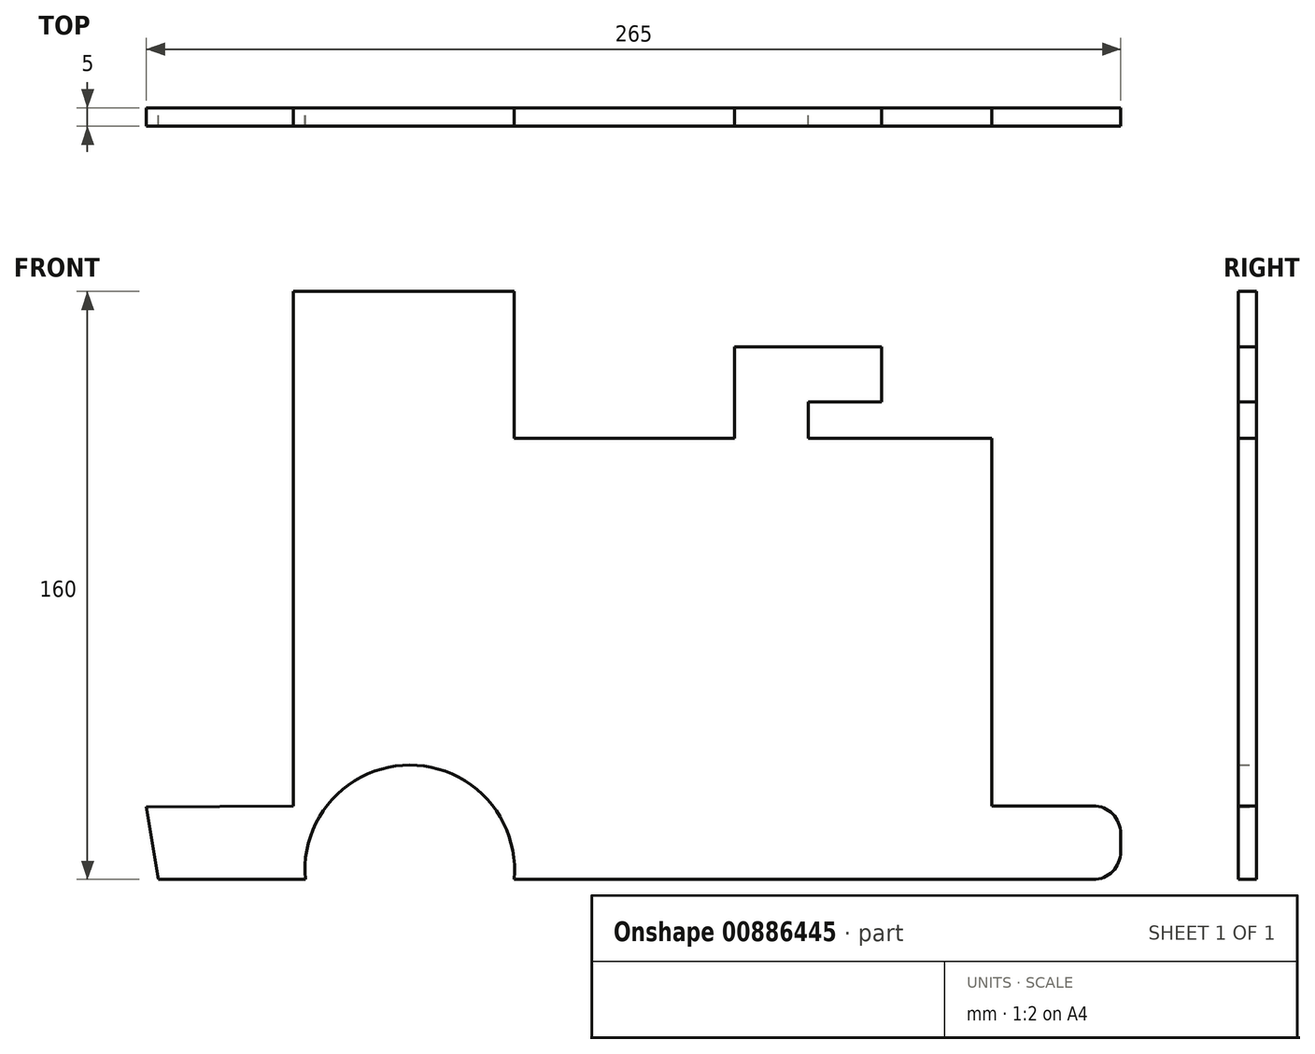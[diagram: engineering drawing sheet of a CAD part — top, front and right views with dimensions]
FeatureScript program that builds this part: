
annotation { "Feature Type Name" : "Feature", "Feature Type Description" : "" }
export const myFeature = defineFeature(function(context is Context, id is Id, definition is map)
    precondition{}
    {
        {
            var Q0;
            Q0=qCreatedBy(makeId("Front.planeOp"),FACE);
            var sketch = newSketch(context, id + "F0", { "sketchPlane" : qUnion([Q0])});
            skLineSegment(sketch, "E0.bottom", {"start": v(-65, 89.5) * mm, "end": v(-5, 89.5) * mm});
            skLineSegment(sketch, "E0.left", {"start": v(-65, 89.5) * mm, "end": v(-65, -50.5) * mm});
            skLineSegment(sketch, "E0.right", {"start": v(-5, 89.5) * mm, "end": v(-5, 49.5) * mm});
            skLineSegment(sketch, "E1", {"start": v(-5, 49.5) * mm, "end": v(55, 49.5) * mm});
            skLineSegment(sketch, "E2", {"start": v(125, 49.5) * mm, "end": v(125, 0) * mm});
            skLineSegment(sketch, "E3", {"start": v(125, -50.5) * mm, "end": v(152.5, -50.5) * mm});
            skLineSegment(sketch, "E4", {"start": v(125, -70.5) * mm, "end": v(152.5, -70.5) * mm});
            skLineSegment(sketch, "E5", {"start": v(160, -63) * mm, "end": v(160, -58) * mm});
            skPoint(sketch, "E6.visualSharp", {"position": v(160, -50.5) * mm});
            skArc(sketch, "E6.filletArc", {"start": v(160, -58) * mm, "mid": v(157.8, -52.7) * mm, "end": v(152.5, -50.5) * mm});
            skPoint(sketch, "E7.visualSharp", {"position": v(160, -70.5) * mm});
            skArc(sketch, "E7.filletArc", {"start": v(152.5, -70.5) * mm, "mid": v(157.8, -68.31) * mm, "end": v(160, -63) * mm});
            skLineSegment(sketch, "E8", {"start": v(125, -70.5) * mm, "end": v(-5, -70.5) * mm});
            skArc(sketch, "E9", {"start": v(-5, -70.5) * mm, "mid": v(-33.38, -39.37) * mm, "end": v(-61.76, -70.5) * mm});
            skLineSegment(sketch, "E10", {"start": v(-61.76, -70.5) * mm, "end": v(-101.76, -70.5) * mm});
            skLineSegment(sketch, "E11", {"start": v(-101.76, -70.5) * mm, "end": v(-105, -50.77) * mm});
            skLineSegment(sketch, "E12", {"start": v(-65, -50.5) * mm, "end": v(-105, -50.77) * mm});
            skPoint(sketch, "E13.orphan", {"position": v(-5, -50.5) * mm});
            skLineSegment(sketch, "E14", {"start": v(55, 49.5) * mm, "end": v(55, 74.5) * mm});
            skLineSegment(sketch, "E15", {"start": v(55, 74.5) * mm, "end": v(95, 74.5) * mm});
            skLineSegment(sketch, "E16", {"start": v(95, 74.5) * mm, "end": v(95, 59.5) * mm});
            skLineSegment(sketch, "E17", {"start": v(75, 49.5) * mm, "end": v(75, 59.5) * mm});
            skLineSegment(sketch, "E18", {"start": v(75, 59.5) * mm, "end": v(95, 59.5) * mm});
            skLineSegment(sketch, "E19.trimOffspring", {"start": v(75, 49.5) * mm, "end": v(125, 49.5) * mm});
            skLineSegment(sketch, "E20", {"start": v(-5, -65.23) * mm, "end": v(-5, -70.5) * mm});
            skLineSegment(sketch, "E21", {"start": v(5, -2.5) * mm, "end": v(120, -2.5) * mm});
            skPoint(sketch, "E22.start.orphan", {"position": v(-5, -5.5) * mm});
            skPoint(sketch, "E23.trimOffspring.end.orphan", {"position": v(125, -2.5) * mm});
            skLineSegment(sketch, "E24", {"start": v(120, 0) * mm, "end": v(5, 0) * mm});
            skPoint(sketch, "E25.end.orphan", {"position": v(120, 0) * mm});
            skLineSegment(sketch, "E26.trimOffspring", {"start": v(125, -2.5) * mm, "end": v(125, -50.5) * mm});
            skPoint(sketch, "E27.end.orphan", {"position": v(5, 0) * mm});
            skPoint(sketch, "E28.orphan", {"position": v(0, -2.5) * mm});
            skPoint(sketch, "E29.orphan", {"position": v(0, 0) * mm});
            skLineSegment(sketch, "E30", {"start": v(125, 0) * mm, "end": v(125, -2.5) * mm});
            skSolve(sketch);
        }
        {
            var Q0;
            Q0=makeQuery(id+"F0.imprint","IMPRINT",FACE,{"disambiguationData":[TD([[makeQuery(id+"F0.imprint","IMPRINT",EDGE,{"derivedFrom":sQuery(id+"F0.wireOp",EDGE,"E0.bottom")}),-1.0]])]});
            extrude(context, id + "F1", {"entities" : qUnion([Q0]), "depth" : 5 * mm, "offsetDistance" : 25 * mm});
        }
    });
